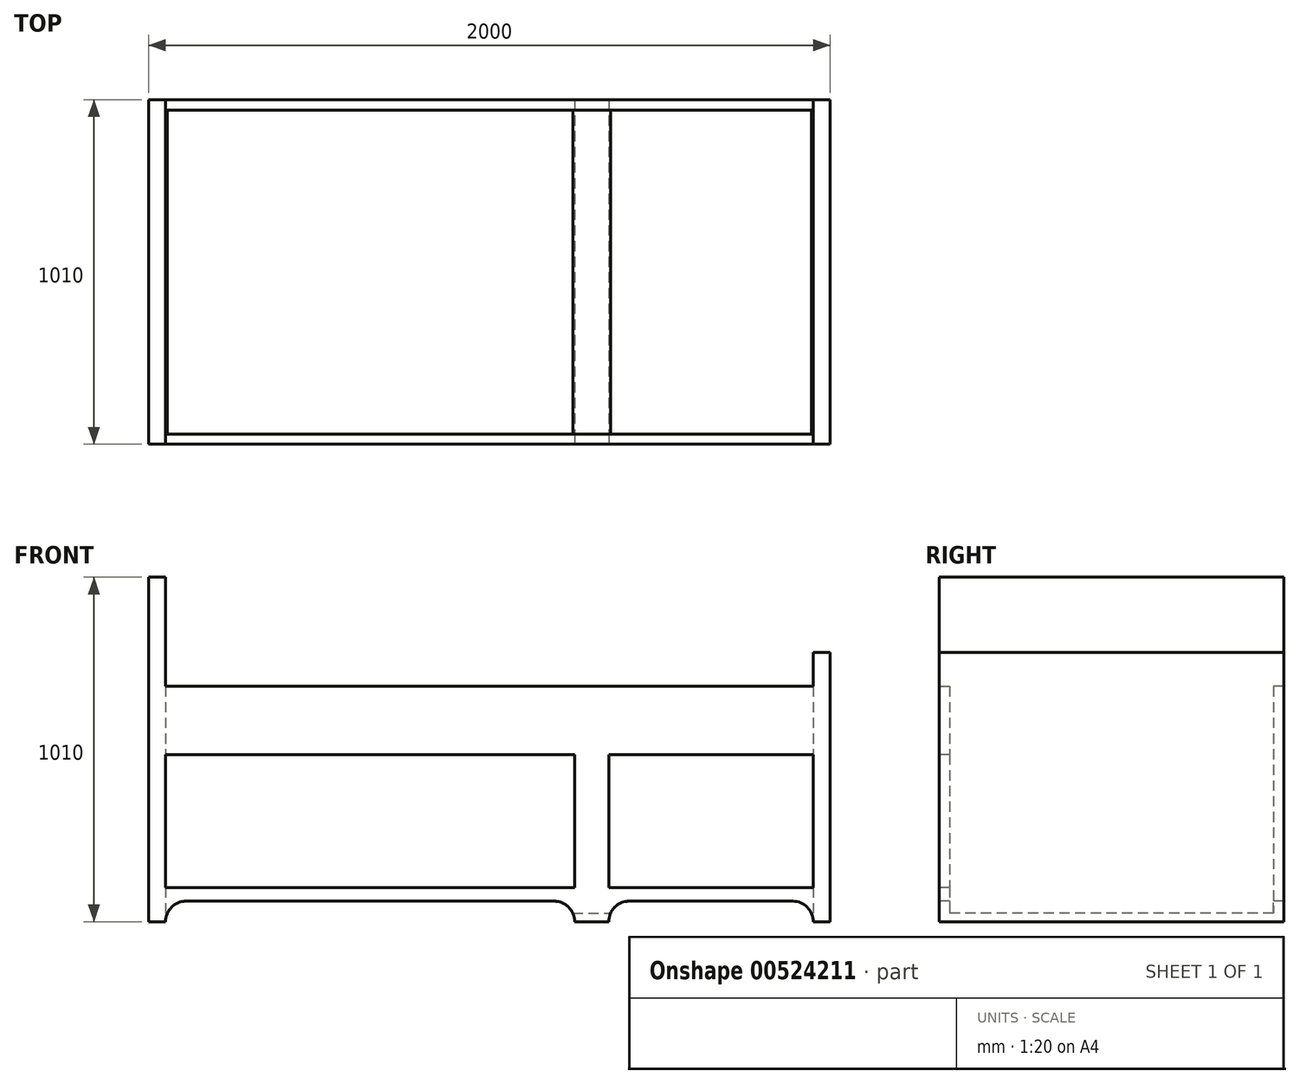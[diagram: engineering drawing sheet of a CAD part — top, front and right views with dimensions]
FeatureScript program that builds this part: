
annotation { "Feature Type Name" : "Feature", "Feature Type Description" : "" }
export const myFeature = defineFeature(function(context is Context, id is Id, definition is map)
    precondition{}
    {
        {
            var Q0;
            Q0=qCreatedBy(makeId("Top.planeOp"),FACE);
            var sketch = newSketch(context, id + "F0", { "sketchPlane" : qUnion([Q0])});
            skLineSegment(sketch, "E0.bottom", {"start": v(-2000, 1010) * mm, "end": v(0, 1010) * mm});
            skLineSegment(sketch, "E0.top", {"start": v(-2000, 0) * mm, "end": v(0, 0) * mm});
            skLineSegment(sketch, "E0.left", {"start": v(-2000, 1010) * mm, "end": v(-2000, 0) * mm});
            skLineSegment(sketch, "E0.right", {"start": v(0, 1010) * mm, "end": v(0, 0) * mm});
            skLineSegment(sketch, "E1.bottom", {"start": v(-2000, 1010) * mm, "end": v(-1950, 1010) * mm});
            skLineSegment(sketch, "E1.top", {"start": v(-2000, 0) * mm, "end": v(-1950, 0) * mm});
            skLineSegment(sketch, "E1.right", {"start": v(-1950, 1010) * mm, "end": v(-1950, 0) * mm});
            skLineSegment(sketch, "E2.bottom", {"start": v(0, 0) * mm, "end": v(-50, 0) * mm});
            skLineSegment(sketch, "E2.top", {"start": v(0, 1010) * mm, "end": v(-50, 1010) * mm});
            skLineSegment(sketch, "E2.left", {"start": v(0, 0) * mm, "end": v(0, 1010) * mm});
            skLineSegment(sketch, "E2.right", {"start": v(-50, 0) * mm, "end": v(-50, 1010) * mm});
            skLineSegment(sketch, "E3.bottom", {"start": v(-1950, 1010) * mm, "end": v(-50, 1010) * mm});
            skLineSegment(sketch, "E3.top", {"start": v(-1950, 980) * mm, "end": v(-50, 980) * mm});
            skLineSegment(sketch, "E3.left", {"start": v(-1950, 1010) * mm, "end": v(-1950, 980) * mm});
            skLineSegment(sketch, "E3.right", {"start": v(-50, 1010) * mm, "end": v(-50, 980) * mm});
            skLineSegment(sketch, "E4.bottom", {"start": v(-1950, 0) * mm, "end": v(-50, 0) * mm});
            skLineSegment(sketch, "E4.top", {"start": v(-1950, 30) * mm, "end": v(-50, 30) * mm});
            skLineSegment(sketch, "E4.left", {"start": v(-1950, 0) * mm, "end": v(-1950, 30) * mm});
            skLineSegment(sketch, "E4.right", {"start": v(-50, 0) * mm, "end": v(-50, 30) * mm});
            skSolve(sketch);
        }
        {
            var Q0;
            {var subQ5=sQuery(id+"F0.wireOp",EDGE,"E3.top");Q0=makeQuery(id+"F0.imprint","IMPRINT",FACE,{"disambiguationData":[TD([[makeQuery(id+"F0.imprint","IMPRINT",EDGE,{"derivedFrom":subQ5}),1.0]])]});}
            var Q1;
            {var subQ5=sQuery(id+"F0.wireOp",EDGE,"E4.top");Q1=makeQuery(id+"F0.imprint","IMPRINT",FACE,{"disambiguationData":[TD([[makeQuery(id+"F0.imprint","IMPRINT",EDGE,{"derivedFrom":subQ5}),-1.0]])]});}
            var Q2;
            {var subQ5=sQuery(id+"F0.wireOp",EDGE,"E0.left");Q2=makeQuery(id+"F0.imprint","IMPRINT",FACE,{"disambiguationData":[TD([[makeQuery(id+"F0.imprint","IMPRINT",EDGE,{"derivedFrom":subQ5}),1.0]])]});}
            var Q3;
            {var subQ3=sQuery(id+"F0.wireOp",EDGE,"E0.right");Q3=makeQuery(id+"F0.imprint","IMPRINT",FACE,{"disambiguationData":[TD([[makeQuery(id+"F0.imprint","IMPRINT",EDGE,{"derivedFrom":subQ3}),-1.0]])]});}
            extrude(context, id + "F1", {"entities" : qUnion([Q0, Q1, Q2, Q3]), "depth" : 690 * mm, "offsetDistance" : 25 * mm});
        }
        {
            var Q0;
            {var subQ5=sQuery(id+"F0.wireOp",EDGE,"E0.left");Q0=makeQuery(id+"F0.imprint","IMPRINT",FACE,{"disambiguationData":[TD([[makeQuery(id+"F0.imprint","IMPRINT",EDGE,{"derivedFrom":subQ5}),1.0]])]});}
            extrude(context, id + "F2", {"entities" : qUnion([Q0]), "operationType" : NewBodyOperationType.ADD, "depth" : 1010 * mm, "offsetDistance" : 25 * mm});
        }
        {
            var Q0;
            {var subQ0=sQuery(id+"F0.wireOp",EDGE,"E3.top");Q0=makeQuery(id+"F0.imprint","IMPRINT",FACE,{"disambiguationData":[TD([[makeQuery(id+"F0.imprint","IMPRINT",EDGE,{"derivedFrom":subQ0}),-1.0]])]});}
            extrude(context, id + "F3", {"entities" : qUnion([Q0]), "operationType" : NewBodyOperationType.ADD, "depth" : 25 * mm, "offsetDistance" : 25 * mm});
        }
        {
            var Q0;
            {var subQ3=sQuery(id+"F0.wireOp",EDGE,"E0.right");Q0=makeQuery(id+"F0.imprint","IMPRINT",FACE,{"disambiguationData":[TD([[makeQuery(id+"F0.imprint","IMPRINT",EDGE,{"derivedFrom":subQ3}),-1.0]])]});}
            extrude(context, id + "F4", {"entities" : qUnion([Q0]), "operationType" : NewBodyOperationType.ADD, "depth" : 790 * mm, "offsetDistance" : 25 * mm});
        }
        {
            var Q0;
            {var subQ0=sQuery(id+"F0.wireOp",EDGE,"E0.top");Q0=makeQuery(id+"F4.boolean.opBoolean","MERGE",FACE,{"derivedFrom":[makeQuery(id+"F2.boolean.opBoolean","MERGE",FACE,{"derivedFrom":[makeQuery(id+"F1.opExtrude","SWEPT_FACE",FACE,{"disambiguationData":[OSD([subQ0])]}),makeQuery(id+"F2.opExtrude","SWEPT_FACE",FACE,{"disambiguationData":[OSD([subQ0])]})]}),makeQuery(id+"F4.opExtrude","SWEPT_FACE",FACE,{"disambiguationData":[OSD([subQ0])]})]});}
            var sketch = newSketch(context, id + "F5", { "sketchPlane" : qUnion([Q0])});
            skLineSegment(sketch, "E5.0.0", {"start": v(0, 0) * mm, "end": v(0, 790) * mm});
            skLineSegment(sketch, "E5.0.1", {"start": v(0, 790) * mm, "end": v(-50, 790) * mm});
            skLineSegment(sketch, "E5.0.2", {"start": v(-50, 790) * mm, "end": v(-50, 690) * mm});
            skLineSegment(sketch, "E5.0.3", {"start": v(-50, 690) * mm, "end": v(-1950, 690) * mm});
            skLineSegment(sketch, "E5.0.4", {"start": v(-1950, 690) * mm, "end": v(-1950, 1010) * mm});
            skLineSegment(sketch, "E5.0.5", {"start": v(-1950, 1010) * mm, "end": v(-2000, 1010) * mm});
            skLineSegment(sketch, "E5.0.6", {"start": v(-2000, 1010) * mm, "end": v(-2000, 0) * mm});
            skLineSegment(sketch, "E5.0.7", {"start": v(-2000, 0) * mm, "end": v(-650, 0) * mm});
            skLineSegment(sketch, "E6.bottom", {"start": v(-1950, 490) * mm, "end": v(-1439.46, 490) * mm});
            skLineSegment(sketch, "E6.top", {"start": v(-1950, 100) * mm, "end": v(-1439.46, 100) * mm});
            skLineSegment(sketch, "E6.left", {"start": v(-1950, 490) * mm, "end": v(-1950, 100) * mm});
            skLineSegment(sketch, "E7.bottom", {"start": v(-1439.46, 490) * mm, "end": v(-750, 490) * mm});
            skLineSegment(sketch, "E7.top", {"start": v(-1439.46, 100) * mm, "end": v(-750, 100) * mm});
            skLineSegment(sketch, "E7.right", {"start": v(-750, 490) * mm, "end": v(-750, 100) * mm});
            skLineSegment(sketch, "E8.bottom", {"start": v(-650, 490) * mm, "end": v(-50, 490) * mm});
            skLineSegment(sketch, "E8.top", {"start": v(-650, 100) * mm, "end": v(-50, 100) * mm});
            skLineSegment(sketch, "E8.left", {"start": v(-650, 490) * mm, "end": v(-650, 100) * mm});
            skLineSegment(sketch, "E8.right", {"start": v(-50, 490) * mm, "end": v(-50, 100) * mm});
            skLineSegment(sketch, "E9", {"start": v(-1890, 60) * mm, "end": v(-810, 60) * mm});
            skLineSegment(sketch, "E10", {"start": v(-590, 60) * mm, "end": v(-110, 60) * mm});
            skArc(sketch, "E11", {"start": v(-50, 0) * mm, "mid": v(-67.57, 42.43) * mm, "end": v(-110, 60) * mm});
            skArc(sketch, "E12", {"start": v(-590, 60) * mm, "mid": v(-632.43, 42.43) * mm, "end": v(-650, 0) * mm});
            skArc(sketch, "E13", {"start": v(-1890, 60) * mm, "mid": v(-1932.43, 42.43) * mm, "end": v(-1950, 0) * mm});
            skArc(sketch, "E14", {"start": v(-750, 0) * mm, "mid": v(-767.57, 42.43) * mm, "end": v(-810, 60) * mm});
            skSolve(sketch);
        }
        {
            var Q0;
            Q0=makeQuery(id+"F5.imprint","IMPRINT",FACE,{"disambiguationData":[TD([[makeQuery(id+"F5.imprint","IMPRINT",EDGE,{"derivedFrom":sQuery(id+"F5.wireOp",EDGE,"E9")}),-1.0]])]});
            var Q1;
            Q1=makeQuery(id+"F5.imprint","IMPRINT",FACE,{"disambiguationData":[TD([[makeQuery(id+"F5.imprint","IMPRINT",EDGE,{"derivedFrom":sQuery(id+"F5.wireOp",EDGE,"E10")}),-1.0]])]});
            extrude(context, id + "F6", {"entities" : qUnion([Q0, Q1]), "operationType" : NewBodyOperationType.REMOVE, "oppositeDirection" : true, "depth" : 1010 * mm, "offsetDistance" : 25 * mm});
        }
        {
            var Q0;
            Q0=makeQuery(id+"F5.imprint","IMPRINT",FACE,{"disambiguationData":[TD([[makeQuery(id+"F5.imprint","IMPRINT",EDGE,{"derivedFrom":sQuery(id+"F5.wireOp",EDGE,"E6.bottom")}),-1.0]])]});
            var Q1;
            Q1=makeQuery(id+"F5.imprint","IMPRINT",FACE,{"disambiguationData":[TD([[makeQuery(id+"F5.imprint","IMPRINT",EDGE,{"derivedFrom":sQuery(id+"F5.wireOp",EDGE,"E8.bottom")}),-1.0]])]});
            extrude(context, id + "F7", {"entities" : qUnion([Q0, Q1]), "operationType" : NewBodyOperationType.REMOVE, "oppositeDirection" : true, "depth" : 30 * mm, "offsetDistance" : 25 * mm});
        }
    });
